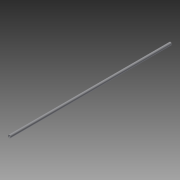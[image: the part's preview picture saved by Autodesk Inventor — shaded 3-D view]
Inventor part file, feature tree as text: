
AUTODESK INVENTOR PART (.ipt)
format: ipt  version: 2013 (Build 170138000, 138)  size: 67,584 bytes
history: native  units: in
note: dims shown in document units (in); Inventor stores cm internally (conversion verified against a paired STEP export)
features: extrude x1, plane x1, sketch x1
ambient origin geometry x8: Origin, YZ Plane, XZ Plane, XY Plane, X Axis, Y Axis, Z Axis, Center Point
bodies: Solid1 (feature_tree)
feature tree (3):
  extrude  "Extrusion1"  Depth=0.091in
  plane  "Work Plane1"
  sketch  "Sketch1"  dims[d0=0.675in d2=0.091in d3=39.75in d4=0.0in]
